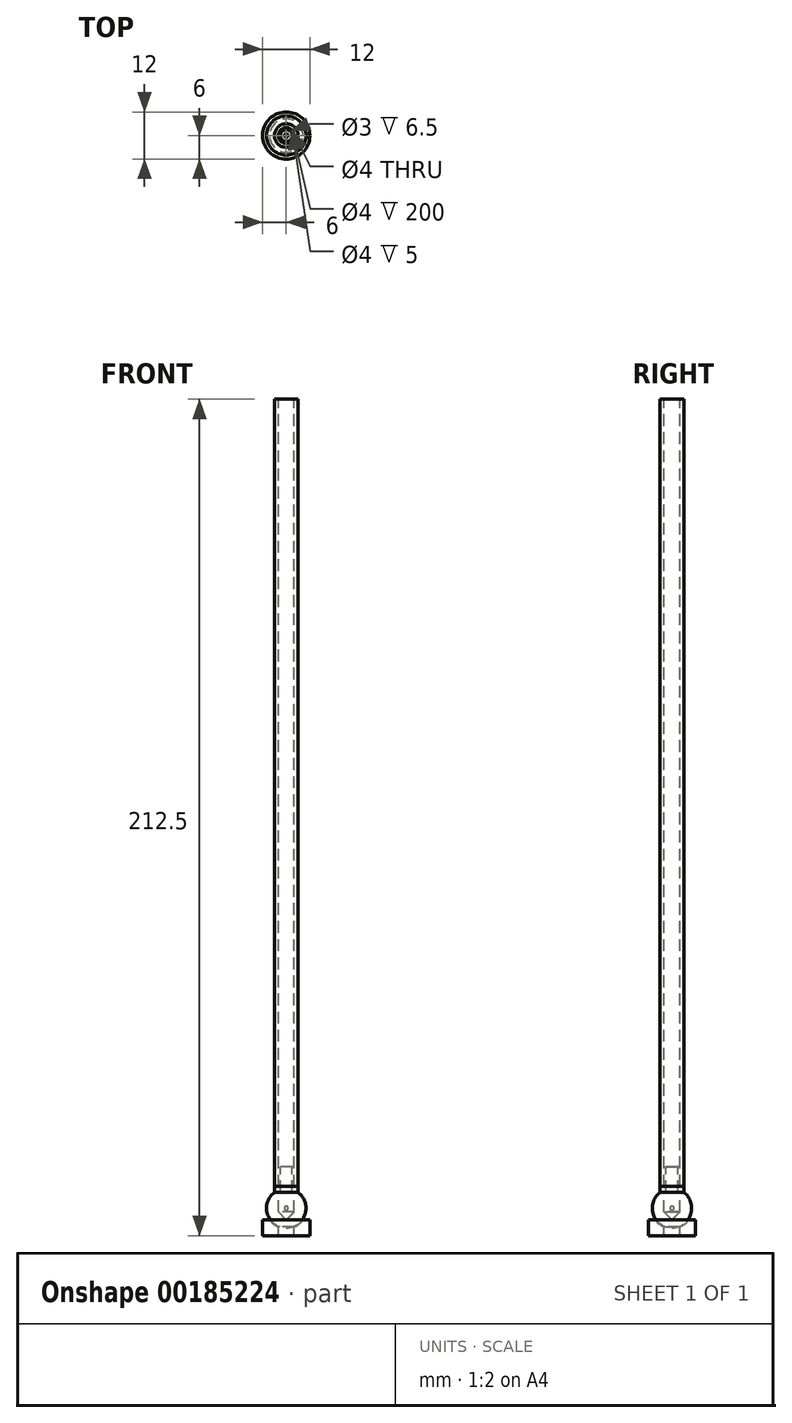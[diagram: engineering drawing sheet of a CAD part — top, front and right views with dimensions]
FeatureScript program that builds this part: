
annotation { "Feature Type Name" : "Feature", "Feature Type Description" : "" }
export const myFeature = defineFeature(function(context is Context, id is Id, definition is map)
    precondition{}
    {
        {
            var Q0;
            Q0=qCreatedBy(makeId("Front.planeOp"),FACE);
            var sketch = newSketch(context, id + "F0", { "sketchPlane" : qUnion([Q0])});
            skArc(sketch, "E0", {"start": v(0, -5) * mm, "mid": v(4.74, -1.58) * mm, "end": v(3, 4) * mm});
            skLineSegment(sketch, "E1", {"start": v(0, -3) * mm, "end": v(0, -5) * mm});
            skLineSegment(sketch, "E2", {"start": v(2, 4) * mm, "end": v(2, -1) * mm});
            skLineSegment(sketch, "E3", {"start": v(2, -1) * mm, "end": v(0, -3) * mm});
            skPoint(sketch, "E4.orphan", {"position": v(0, 5) * mm});
            skLineSegment(sketch, "E5", {"start": v(2, 4) * mm, "end": v(3, 4) * mm});
            skLineSegment(sketch, "E6", {"start": v(4.25, -3) * mm, "end": v(6, -3) * mm});
            skLineSegment(sketch, "E7", {"start": v(6, -3) * mm, "end": v(6, -7) * mm});
            skLineSegment(sketch, "E8", {"start": v(6, -7) * mm, "end": v(2, -7) * mm});
            skLineSegment(sketch, "E9", {"start": v(2, -7) * mm, "end": v(2, -4.8) * mm});
            skLineSegment(sketch, "E10.bottom", {"start": v(2, 205.5) * mm, "end": v(3, 205.5) * mm});
            skLineSegment(sketch, "E10.top", {"start": v(2, 5.5) * mm, "end": v(3, 5.5) * mm});
            skLineSegment(sketch, "E10.left", {"start": v(2, 205.5) * mm, "end": v(2, 5.5) * mm});
            skLineSegment(sketch, "E10.right", {"start": v(3, 205.5) * mm, "end": v(3, 5.5) * mm});
            skLineSegment(sketch, "E11", {"start": v(3, 5.5) * mm, "end": v(3, 4) * mm});
            skLineSegment(sketch, "E12", {"start": v(3, 4) * mm, "end": v(1.5, 4) * mm});
            skLineSegment(sketch, "E13", {"start": v(1.5, 4) * mm, "end": v(1.5, 10.5) * mm});
            skLineSegment(sketch, "E14", {"start": v(1.5, 10.5) * mm, "end": v(2, 10.5) * mm});
            skArc(sketch, "E15.trimOffspring", {"start": v(2, -4.8) * mm, "mid": v(3.25, -4.06) * mm, "end": v(4.25, -3) * mm});
            skArc(sketch, "E16", {"start": v(0, -0.5) * mm, "mid": v(0.5, 0) * mm, "end": v(0, 0.5) * mm});
            skLineSegment(sketch, "E17", {"start": v(0, 0.5) * mm, "end": v(0, -0.5) * mm});
            skSolve(sketch);
        }
        {
            var Q0;
            Q0=makeQuery(id+"F0.imprint","IMPRINT",FACE,{"disambiguationData":[TD([[makeQuery(id+"F0.imprint","IMPRINT",EDGE,{"derivedFrom":sQuery(id+"F0.wireOp",EDGE,"E0")}),1.0]])]});
            var Q1;
            Q1=sQuery(id+"F0.wireOp",EDGE,"E1");
            revolve(context, id + "F1", {"entities" : qUnion([Q0]), "axis" : qUnion([Q1]), "revolveType" : RevolveType.FULL});
        }
        {
            var Q0;
            {var subQ0=sQuery(id+"F0.wireOp",EDGE,"E6");Q0=makeQuery(id+"F0.imprint","IMPRINT",FACE,{"disambiguationData":[TD([[makeQuery(id+"F0.imprint","IMPRINT",EDGE,{"derivedFrom":subQ0}),-1.0]])]});}
            var Q1;
            Q1=sQuery(id+"F0.wireOp",EDGE,"E1");
            revolve(context, id + "F2", {"entities" : qUnion([Q0]), "axis" : qUnion([Q1]), "revolveType" : RevolveType.FULL});
        }
        {
            var Q0;
            Q0=makeQuery(id+"F0.imprint","IMPRINT",FACE,{"disambiguationData":[TD([[makeQuery(id+"F0.imprint","IMPRINT",EDGE,{"derivedFrom":sQuery(id+"F0.wireOp",EDGE,"E10.bottom")}),-1.0]])]});
            var Q1;
            Q1=sQuery(id+"F0.wireOp",EDGE,"E1");
            revolve(context, id + "F3", {"entities" : qUnion([Q0]), "axis" : qUnion([Q1]), "revolveType" : RevolveType.FULL});
        }
        {
            var Q0;
            {var subQ3=sQuery(id+"F0.wireOp",EDGE,"E10.top");Q0=makeQuery(id+"F0.imprint","IMPRINT",FACE,{"disambiguationData":[TD([[makeQuery(id+"F0.imprint","IMPRINT",EDGE,{"derivedFrom":subQ3}),-1.0]])]});}
            var Q1;
            Q1=sQuery(id+"F0.wireOp",EDGE,"E1");
            revolve(context, id + "F4", {"entities" : qUnion([Q0]), "axis" : qUnion([Q1]), "revolveType" : RevolveType.FULL});
        }
        {
            var Q0;
            Q0=makeQuery(id+"F0.imprint","IMPRINT",FACE,{"disambiguationData":[TD([[makeQuery(id+"F0.imprint","IMPRINT",EDGE,{"derivedFrom":sQuery(id+"F0.wireOp",EDGE,"E16")}),1.0]])]});
            var Q1;
            Q1=sQuery(id+"F0.wireOp",EDGE,"E17");
            revolve(context, id + "F5", {"entities" : qUnion([Q0]), "axis" : qUnion([Q1]), "revolveType" : RevolveType.FULL});
        }
    });
